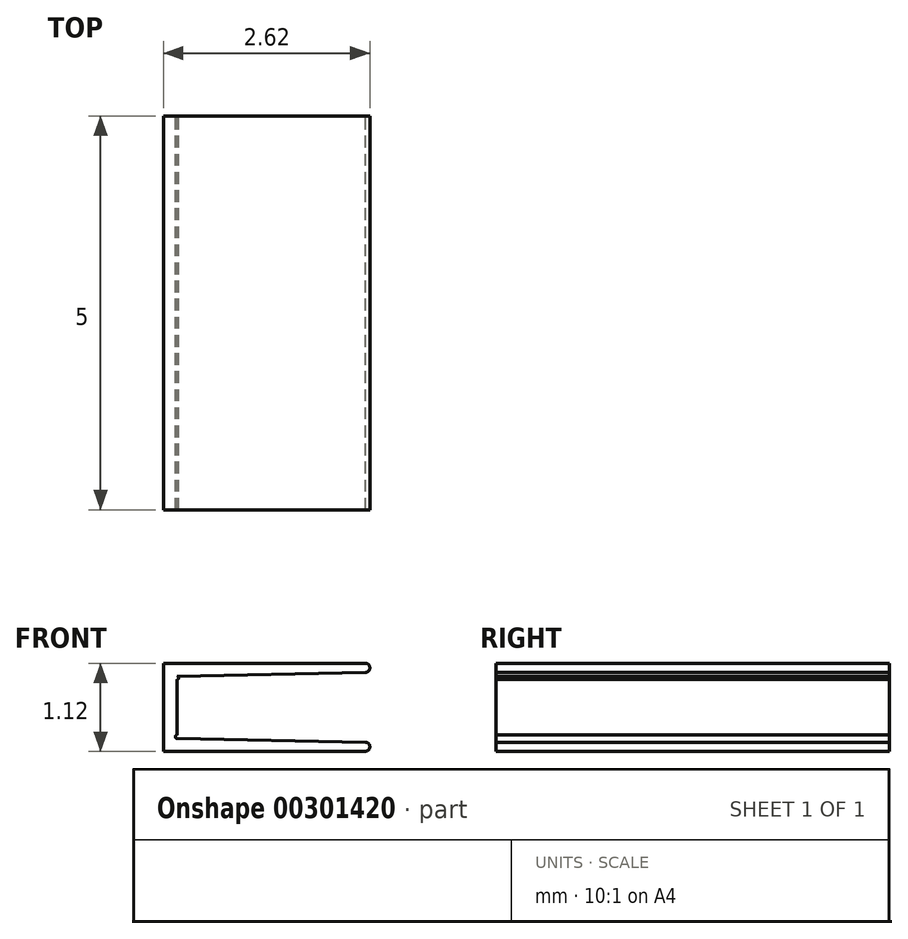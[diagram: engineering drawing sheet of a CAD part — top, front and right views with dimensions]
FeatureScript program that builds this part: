
annotation { "Feature Type Name" : "Feature", "Feature Type Description" : "" }
export const myFeature = defineFeature(function(context is Context, id is Id, definition is map)
    precondition{}
    {
        {
            var Q0;
            Q0=qCreatedBy(makeId("Front.planeOp"),FACE);
            var sketch = newSketch(context, id + "F0", { "sketchPlane" : qUnion([Q0])});
            skLineSegment(sketch, "E0", {"start": v(-0.16, 0.56) * mm, "end": v(-2.72, 0.56) * mm});
            skArc(sketch, "E1", {"start": v(-0.16, 0.44) * mm, "mid": v(-0.1, 0.5) * mm, "end": v(-0.16, 0.56) * mm});
            skLineSegment(sketch, "E2", {"start": v(-0.16, 0.44) * mm, "end": v(-2.55, 0.4) * mm});
            skArc(sketch, "E3", {"start": v(-2.55, 0.4) * mm, "mid": v(-2.53, 0.37) * mm, "end": v(-2.55, 0.35) * mm});
            skLineSegment(sketch, "E4", {"start": v(-2.55, 0.35) * mm, "end": v(-2.55, 0) * mm});
            skLineSegment(sketch, "E5.MirrorCS", {"start": v(-2.55, -0.35) * mm, "end": v(-2.55, 0) * mm});
            skLineSegment(sketch, "E6.MirrorCS", {"start": v(-0.16, -0.44) * mm, "end": v(-2.55, -0.4) * mm});
            skLineSegment(sketch, "E7.MirrorCS", {"start": v(-0.16, -0.56) * mm, "end": v(-2.72, -0.56) * mm});
            skArc(sketch, "E8.MirrorCS", {"start": v(-2.55, -0.4) * mm, "mid": v(-2.57, -0.37) * mm, "end": v(-2.55, -0.35) * mm});
            skArc(sketch, "E9.MirrorCS", {"start": v(-0.16, -0.44) * mm, "mid": v(-0.1, -0.5) * mm, "end": v(-0.16, -0.56) * mm});
            skLineSegment(sketch, "E10", {"start": v(-2.72, 0.56) * mm, "end": v(-2.72, -0.56) * mm});
            skSolve(sketch);
        }
        {
            var Q0;
            Q0 = qSketchRegion(id + "F0", true);
            extrude(context, id + "F1", {"entities" : qUnion([Q0]), "depth" : 5 * mm});
        }
    });
